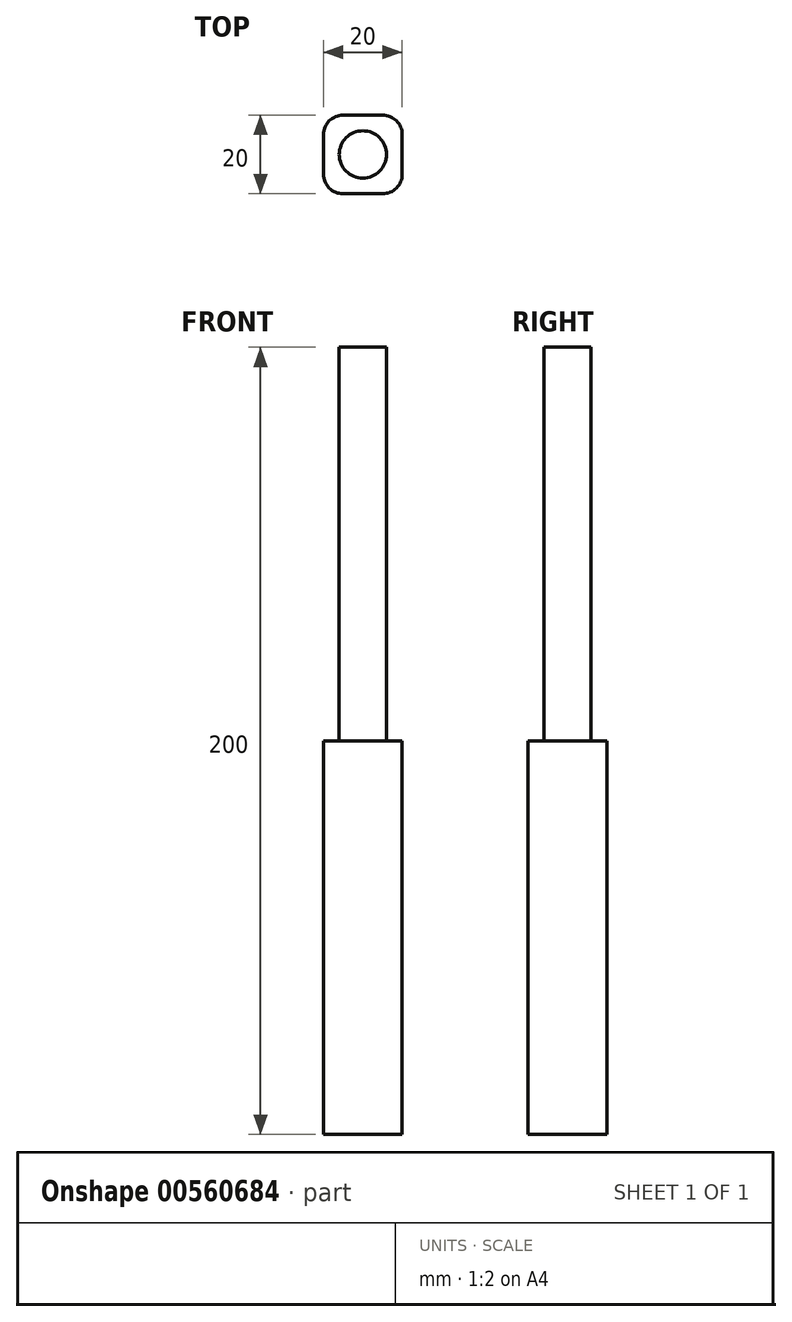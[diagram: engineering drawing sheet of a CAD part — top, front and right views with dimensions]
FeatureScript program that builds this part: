
annotation { "Feature Type Name" : "Feature", "Feature Type Description" : "" }
export const myFeature = defineFeature(function(context is Context, id is Id, definition is map)
    precondition{}
    {
        {
            var Q0;
            Q0=qCreatedBy(makeId("Top.planeOp"),FACE);
            var sketch = newSketch(context, id + "F0", { "sketchPlane" : qUnion([Q0])});
            skCircle(sketch, "E0", {"center": v(0, 0) * mm, "radius": 6 * mm});
            skSolve(sketch);
        }
        {
            var Q0;
            Q0=makeQuery(id+"F0.imprint","IMPRINT",FACE,{"disambiguationData":[TD([[makeQuery(id+"F0.imprint","IMPRINT",EDGE,{"derivedFrom":sQuery(id+"F0.wireOp",EDGE,"E0")}),1.0]])]});
            extrude(context, id + "F1", {"entities" : qUnion([Q0]), "depth" : 100 * mm, "offsetDistance" : 25 * mm});
        }
        {
            var Q0;
            Q0=makeQuery(id+"F1.opExtrude","CAP_FACE",FACE,{"disambiguationData":[OSD([sQuery(id+"F0.wireOp",EDGE,"E0")])],"isStart":true});
            var sketch = newSketch(context, id + "F2", { "sketchPlane" : qUnion([Q0])});
            skLineSegment(sketch, "E1", {"start": v(-6, 0) * mm, "end": v(-10, 0) * mm});
            skLineSegment(sketch, "E2", {"start": v(0, -6) * mm, "end": v(0, -10) * mm});
            skLineSegment(sketch, "E3", {"start": v(6, 0) * mm, "end": v(10, 0) * mm});
            skLineSegment(sketch, "E4", {"start": v(0, 6) * mm, "end": v(0, 10) * mm});
            skLineSegment(sketch, "E5.bottom", {"start": v(5, -10) * mm, "end": v(-5, -10) * mm});
            skLineSegment(sketch, "E5.top", {"start": v(5, 10) * mm, "end": v(-5, 10) * mm});
            skLineSegment(sketch, "E5.left", {"start": v(10, -5) * mm, "end": v(10, 5) * mm});
            skLineSegment(sketch, "E5.right", {"start": v(-10, -5) * mm, "end": v(-10, 5) * mm});
            skPoint(sketch, "E6.visualSharp", {"position": v(10, -10) * mm});
            skArc(sketch, "E6.filletArc", {"start": v(5, -10) * mm, "mid": v(8.54, -8.54) * mm, "end": v(10, -5) * mm});
            skPoint(sketch, "E7.visualSharp", {"position": v(-10, -10) * mm});
            skArc(sketch, "E7.filletArc", {"start": v(-10, -5) * mm, "mid": v(-8.54, -8.54) * mm, "end": v(-5, -10) * mm});
            skPoint(sketch, "E8.visualSharp", {"position": v(-10, 10) * mm});
            skArc(sketch, "E8.filletArc", {"start": v(-5, 10) * mm, "mid": v(-8.54, 8.54) * mm, "end": v(-10, 5) * mm});
            skPoint(sketch, "E9.visualSharp", {"position": v(10, 10) * mm});
            skArc(sketch, "E9.filletArc", {"start": v(10, 5) * mm, "mid": v(8.54, 8.54) * mm, "end": v(5, 10) * mm});
            skSolve(sketch);
        }
        {
            var Q0;
            {var subQ2=sQuery(id+"F2.wireOp",EDGE,"E1");Q0=makeQuery(id+"F2.imprint","IMPRINT",FACE,{"disambiguationData":[TD([[makeQuery(id+"F2.imprint","IMPRINT",EDGE,{"derivedFrom":subQ2}),1.0]])]});}
            var Q1;
            {var subQ1=sQuery(id+"F2.wireOp",EDGE,"E1");Q1=makeQuery(id+"F2.imprint","IMPRINT",FACE,{"disambiguationData":[TD([[makeQuery(id+"F2.imprint","IMPRINT",EDGE,{"derivedFrom":subQ1}),-1.0]])]});}
            var Q2;
            {var subQ1=sQuery(id+"F2.wireOp",EDGE,"E3");Q2=makeQuery(id+"F2.imprint","IMPRINT",FACE,{"disambiguationData":[TD([[makeQuery(id+"F2.imprint","IMPRINT",EDGE,{"derivedFrom":subQ1}),1.0]])]});}
            var Q3;
            {var subQ0=makeQuery(id+"F1.opExtrude","CAP_EDGE",EDGE,{"disambiguationData":[OSD([sQuery(id+"F0.wireOp",EDGE,"E0")])],"isStart":true});var subQ1=makeQuery(id+"F2.imprint","INTERSECT",VERTEX,{"derivedFrom":[subQ0,sQuery(id+"F2.wireOp",EDGE,"E1")]});Q3=makeQuery(id+"F2.imprint","IMPRINT",FACE,{"disambiguationData":[TD([[makeQuery(id+"F2.imprint","IMPRINT",EDGE,{"disambiguationData":[TD([[subQ1,1.0]])],"derivedFrom":subQ0}),-1.0]])]});}
            var Q4;
            {var subQ4=sQuery(id+"F2.wireOp",EDGE,"E2");Q4=makeQuery(id+"F2.imprint","IMPRINT",FACE,{"disambiguationData":[TD([[makeQuery(id+"F2.imprint","IMPRINT",EDGE,{"derivedFrom":subQ4}),1.0]])]});}
            extrude(context, id + "F3", {"entities" : qUnion([Q0, Q1, Q2, Q3, Q4]), "operationType" : NewBodyOperationType.ADD, "depth" : 100 * mm, "offsetDistance" : 25 * mm});
        }
    });
